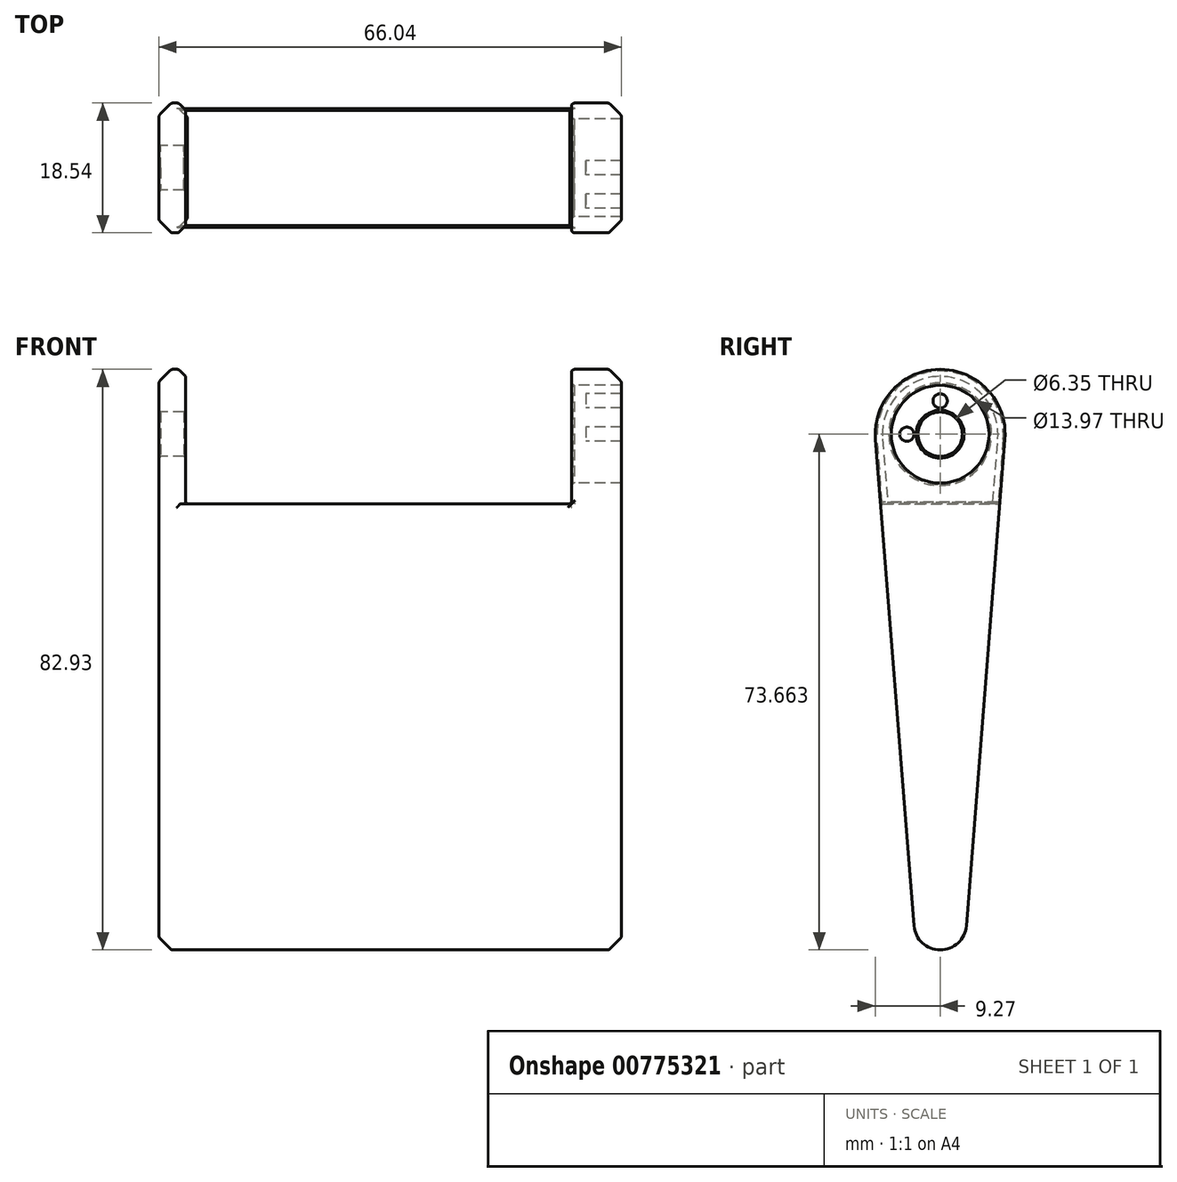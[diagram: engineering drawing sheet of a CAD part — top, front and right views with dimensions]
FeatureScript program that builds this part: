
annotation { "Feature Type Name" : "Feature", "Feature Type Description" : "" }
export const myFeature = defineFeature(function(context is Context, id is Id, definition is map)
    precondition{}
    {
        {
            var Q0;
            Q0=qCreatedBy(makeId("Right.planeOp"),FACE);
            var sketch = newSketch(context, id + "F0", { "sketchPlane" : qUnion([Q0])});
            skCircle(sketch, "E0", {"center": v(0, 54.12) * mm, "radius": 9.27 * mm});
            skCircle(sketch, "E1", {"center": v(0, -15.79) * mm, "radius": 3.75 * mm});
            skCircle(sketch, "E2", {"center": v(0, 54.12) * mm, "radius": 6.99 * mm});
            skCircle(sketch, "E3", {"center": v(0, 54.12) * mm, "radius": 3.18 * mm});
            skLineSegment(sketch, "E4", {"start": v(-9.24, 53.4) * mm, "end": v(-3.74, -16.08) * mm});
            skLineSegment(sketch, "E5", {"start": v(9.24, 53.4) * mm, "end": v(3.74, -16.08) * mm});
            skSolve(sketch);
        }
        {
            var Q0;
            {var subQ0=sQuery(id+"F0.wireOp",EDGE,"E4");Q0=makeQuery(id+"F0.imprint","IMPRINT",FACE,{"disambiguationData":[TD([[makeQuery(id+"F0.imprint","IMPRINT",EDGE,{"derivedFrom":subQ0}),1.0]])]});}
            var Q1;
            Q1=makeQuery(id+"F0.imprint","IMPRINT",FACE,{"disambiguationData":[TD([[makeQuery(id+"F0.imprint","IMPRINT",EDGE,{"derivedFrom":sQuery(id+"F0.wireOp",EDGE,"E2")}),-1.0]])]});
            var Q2;
            Q2=makeQuery(id+"F0.imprint","IMPRINT",FACE,{"disambiguationData":[TD([[makeQuery(id+"F0.imprint","IMPRINT",EDGE,{"derivedFrom":sQuery(id+"F0.wireOp",EDGE,"E2")}),1.0]])]});
            var Q3;
            {var subQ0=sQuery(id+"F0.wireOp",EDGE,"E1");var subQ1=makeQuery(id+"F0.imprint","INTERSECT",VERTEX,{"derivedFrom":[subQ0,sQuery(id+"F0.wireOp",EDGE,"E4")]});Q3=makeQuery(id+"F0.imprint","IMPRINT",FACE,{"disambiguationData":[TD([[makeQuery(id+"F0.imprint","IMPRINT",EDGE,{"disambiguationData":[TD([[subQ1,-1.0]])],"derivedFrom":subQ0}),1.0]])]});}
            extrude(context, id + "F1", {"entities" : qUnion([Q0, Q1, Q2, Q3]), "depth" : 66.04 * mm, "offsetDistance" : 25.4 * mm});
        }
        {
            var Q0;
            Q0=makeQuery(id+"F0.imprint","IMPRINT",FACE,{"disambiguationData":[TD([[makeQuery(id+"F0.imprint","IMPRINT",EDGE,{"derivedFrom":sQuery(id+"F0.wireOp",EDGE,"E2")}),-1.0]])]});
            var Q1;
            Q1=makeQuery(id+"F0.imprint","IMPRINT",FACE,{"disambiguationData":[TD([[makeQuery(id+"F0.imprint","IMPRINT",EDGE,{"derivedFrom":sQuery(id+"F0.wireOp",EDGE,"E2")}),1.0]])]});
            extrude(context, id + "F2", {"entities" : qUnion([Q0, Q1]), "operationType" : NewBodyOperationType.REMOVE, "depth" : 56.4 * mm, "offsetDistance" : 25.4 * mm});
        }
        {
            var Q0;
            Q0=makeQuery(id+"F0.imprint","IMPRINT",FACE,{"disambiguationData":[TD([[makeQuery(id+"F0.imprint","IMPRINT",EDGE,{"derivedFrom":sQuery(id+"F0.wireOp",EDGE,"E2")}),1.0]])]});
            extrude(context, id + "F3", {"entities" : qUnion([Q0]), "operationType" : NewBodyOperationType.REMOVE, "depth" : 60.96 * mm, "offsetDistance" : 25.4 * mm});
        }
        {
            var Q0;
            Q0=makeQuery(id+"F3.boolean.opBoolean","COPY",FACE,{"derivedFrom":makeQuery(id+"F3.opExtrude","CAP_FACE",FACE,{"disambiguationData":[OSD([sQuery(id+"F0.wireOp",EDGE,"E2"),sQuery(id+"F0.wireOp",EDGE,"E3")])],"isStart":false})});
            var sketch = newSketch(context, id + "F4", { "sketchPlane" : qUnion([Q0])});
            skCircle(sketch, "E6", {"center": v(0, 54.12) * mm, "radius": 4.76 * mm});
            skCircle(sketch, "E7", {"center": v(4.76, 54.12) * mm, "radius": 1.02 * mm});
            skCircle(sketch, "E8.1.0", {"center": v(3.37, 57.49) * mm, "radius": 1.02 * mm});
            skCircle(sketch, "E8.2.0", {"center": v(0, 58.88) * mm, "radius": 1.02 * mm});
            skCircle(sketch, "E8.3.0", {"center": v(-3.37, 57.49) * mm, "radius": 1.02 * mm});
            skCircle(sketch, "E8.4.0", {"center": v(-4.76, 54.12) * mm, "radius": 1.02 * mm});
            skCircle(sketch, "E8.5.0", {"center": v(-3.37, 50.76) * mm, "radius": 1.02 * mm});
            skCircle(sketch, "E8.6.0", {"center": v(0, 49.36) * mm, "radius": 1.02 * mm});
            skCircle(sketch, "E8.7.0", {"center": v(3.37, 50.76) * mm, "radius": 1.02 * mm});
            skLineSegment(sketch, "E8.anchor1", {"start": v(0, 54.12) * mm, "end": v(4.76, 54.12) * mm, "construction": true});
            skLineSegment(sketch, "E8.anchor2", {"start": v(0, 54.12) * mm, "end": v(3.37, 50.76) * mm, "construction": true});
            skSolve(sketch);
        }
        {
            var Q0;
            {var subQ0=sQuery(id+"F4.wireOp",EDGE,"E7");var subQ1=sQuery(id+"F4.wireOp",EDGE,"E6");var subQ2=makeQuery(id+"F4.imprint","INTERSECT",VERTEX,{"disambiguationData":[OD(0.0)],"derivedFrom":[subQ1,subQ0]});Q0=makeQuery(id+"F4.imprint","IMPRINT",FACE,{"disambiguationData":[TD([[makeQuery(id+"F4.imprint","IMPRINT",EDGE,{"disambiguationData":[TD([[subQ2,1.0]])],"derivedFrom":subQ1}),-1.0]])]});}
            var Q1;
            {var subQ0=sQuery(id+"F4.wireOp",EDGE,"E7");var subQ1=sQuery(id+"F4.wireOp",EDGE,"E6");var subQ2=makeQuery(id+"F4.imprint","INTERSECT",VERTEX,{"disambiguationData":[OD(0.0)],"derivedFrom":[subQ1,subQ0]});Q1=makeQuery(id+"F4.imprint","IMPRINT",FACE,{"disambiguationData":[TD([[makeQuery(id+"F4.imprint","IMPRINT",EDGE,{"disambiguationData":[TD([[subQ2,1.0]])],"derivedFrom":subQ1}),1.0]])]});}
            var Q2;
            {var subQ0=sQuery(id+"F4.wireOp",EDGE,"E8.1.0");var subQ1=sQuery(id+"F4.wireOp",EDGE,"E6");var subQ2=makeQuery(id+"F4.imprint","INTERSECT",VERTEX,{"disambiguationData":[OD(0.0)],"derivedFrom":[subQ1,subQ0]});Q2=makeQuery(id+"F4.imprint","IMPRINT",FACE,{"disambiguationData":[TD([[makeQuery(id+"F4.imprint","IMPRINT",EDGE,{"disambiguationData":[TD([[subQ2,-1.0]])],"derivedFrom":subQ1}),-1.0]])]});}
            var Q3;
            {var subQ0=sQuery(id+"F4.wireOp",EDGE,"E8.1.0");var subQ1=sQuery(id+"F4.wireOp",EDGE,"E6");var subQ2=makeQuery(id+"F4.imprint","INTERSECT",VERTEX,{"disambiguationData":[OD(0.0)],"derivedFrom":[subQ1,subQ0]});Q3=makeQuery(id+"F4.imprint","IMPRINT",FACE,{"disambiguationData":[TD([[makeQuery(id+"F4.imprint","IMPRINT",EDGE,{"disambiguationData":[TD([[subQ2,-1.0]])],"derivedFrom":subQ1}),1.0]])]});}
            var Q4;
            {var subQ0=sQuery(id+"F4.wireOp",EDGE,"E8.2.0");var subQ1=sQuery(id+"F4.wireOp",EDGE,"E6");var subQ2=makeQuery(id+"F4.imprint","INTERSECT",VERTEX,{"disambiguationData":[OD(0.0)],"derivedFrom":[subQ1,subQ0]});Q4=makeQuery(id+"F4.imprint","IMPRINT",FACE,{"disambiguationData":[TD([[makeQuery(id+"F4.imprint","IMPRINT",EDGE,{"disambiguationData":[TD([[subQ2,-1.0]])],"derivedFrom":subQ1}),1.0]])]});}
            var Q5;
            {var subQ0=sQuery(id+"F4.wireOp",EDGE,"E8.2.0");var subQ1=sQuery(id+"F4.wireOp",EDGE,"E6");var subQ2=makeQuery(id+"F4.imprint","INTERSECT",VERTEX,{"disambiguationData":[OD(0.0)],"derivedFrom":[subQ1,subQ0]});Q5=makeQuery(id+"F4.imprint","IMPRINT",FACE,{"disambiguationData":[TD([[makeQuery(id+"F4.imprint","IMPRINT",EDGE,{"disambiguationData":[TD([[subQ2,-1.0]])],"derivedFrom":subQ1}),-1.0]])]});}
            var Q6;
            {var subQ0=sQuery(id+"F4.wireOp",EDGE,"E8.3.0");var subQ1=sQuery(id+"F4.wireOp",EDGE,"E6");var subQ2=makeQuery(id+"F4.imprint","INTERSECT",VERTEX,{"disambiguationData":[OD(0.0)],"derivedFrom":[subQ1,subQ0]});Q6=makeQuery(id+"F4.imprint","IMPRINT",FACE,{"disambiguationData":[TD([[makeQuery(id+"F4.imprint","IMPRINT",EDGE,{"disambiguationData":[TD([[subQ2,-1.0]])],"derivedFrom":subQ1}),1.0]])]});}
            var Q7;
            {var subQ0=sQuery(id+"F4.wireOp",EDGE,"E8.3.0");var subQ1=sQuery(id+"F4.wireOp",EDGE,"E6");var subQ2=makeQuery(id+"F4.imprint","INTERSECT",VERTEX,{"disambiguationData":[OD(0.0)],"derivedFrom":[subQ1,subQ0]});Q7=makeQuery(id+"F4.imprint","IMPRINT",FACE,{"disambiguationData":[TD([[makeQuery(id+"F4.imprint","IMPRINT",EDGE,{"disambiguationData":[TD([[subQ2,-1.0]])],"derivedFrom":subQ1}),-1.0]])]});}
            var Q8;
            {var subQ0=sQuery(id+"F4.wireOp",EDGE,"E8.4.0");var subQ1=sQuery(id+"F4.wireOp",EDGE,"E6");var subQ2=makeQuery(id+"F4.imprint","INTERSECT",VERTEX,{"disambiguationData":[OD(0.0)],"derivedFrom":[subQ1,subQ0]});Q8=makeQuery(id+"F4.imprint","IMPRINT",FACE,{"disambiguationData":[TD([[makeQuery(id+"F4.imprint","IMPRINT",EDGE,{"disambiguationData":[TD([[subQ2,-1.0]])],"derivedFrom":subQ1}),1.0]])]});}
            var Q9;
            {var subQ0=sQuery(id+"F4.wireOp",EDGE,"E8.4.0");var subQ1=sQuery(id+"F4.wireOp",EDGE,"E6");var subQ2=makeQuery(id+"F4.imprint","INTERSECT",VERTEX,{"disambiguationData":[OD(0.0)],"derivedFrom":[subQ1,subQ0]});Q9=makeQuery(id+"F4.imprint","IMPRINT",FACE,{"disambiguationData":[TD([[makeQuery(id+"F4.imprint","IMPRINT",EDGE,{"disambiguationData":[TD([[subQ2,-1.0]])],"derivedFrom":subQ1}),-1.0]])]});}
            var Q10;
            {var subQ0=sQuery(id+"F4.wireOp",EDGE,"E8.5.0");var subQ1=sQuery(id+"F4.wireOp",EDGE,"E6");var subQ2=makeQuery(id+"F4.imprint","INTERSECT",VERTEX,{"disambiguationData":[OD(0.0)],"derivedFrom":[subQ1,subQ0]});Q10=makeQuery(id+"F4.imprint","IMPRINT",FACE,{"disambiguationData":[TD([[makeQuery(id+"F4.imprint","IMPRINT",EDGE,{"disambiguationData":[TD([[subQ2,-1.0]])],"derivedFrom":subQ1}),1.0]])]});}
            var Q11;
            {var subQ0=sQuery(id+"F4.wireOp",EDGE,"E8.5.0");var subQ1=sQuery(id+"F4.wireOp",EDGE,"E6");var subQ2=makeQuery(id+"F4.imprint","INTERSECT",VERTEX,{"disambiguationData":[OD(0.0)],"derivedFrom":[subQ1,subQ0]});Q11=makeQuery(id+"F4.imprint","IMPRINT",FACE,{"disambiguationData":[TD([[makeQuery(id+"F4.imprint","IMPRINT",EDGE,{"disambiguationData":[TD([[subQ2,-1.0]])],"derivedFrom":subQ1}),-1.0]])]});}
            var Q12;
            {var subQ0=sQuery(id+"F4.wireOp",EDGE,"E8.6.0");var subQ1=sQuery(id+"F4.wireOp",EDGE,"E6");var subQ2=makeQuery(id+"F4.imprint","INTERSECT",VERTEX,{"disambiguationData":[OD(0.0)],"derivedFrom":[subQ1,subQ0]});Q12=makeQuery(id+"F4.imprint","IMPRINT",FACE,{"disambiguationData":[TD([[makeQuery(id+"F4.imprint","IMPRINT",EDGE,{"disambiguationData":[TD([[subQ2,-1.0]])],"derivedFrom":subQ1}),1.0]])]});}
            var Q13;
            {var subQ0=sQuery(id+"F4.wireOp",EDGE,"E8.7.0");var subQ1=sQuery(id+"F4.wireOp",EDGE,"E6");var subQ2=makeQuery(id+"F4.imprint","INTERSECT",VERTEX,{"disambiguationData":[OD(0.0)],"derivedFrom":[subQ1,subQ0]});Q13=makeQuery(id+"F4.imprint","IMPRINT",FACE,{"disambiguationData":[TD([[makeQuery(id+"F4.imprint","IMPRINT",EDGE,{"disambiguationData":[TD([[subQ2,-1.0]])],"derivedFrom":subQ1}),1.0]])]});}
            var Q14;
            {var subQ0=sQuery(id+"F4.wireOp",EDGE,"E8.7.0");var subQ1=sQuery(id+"F4.wireOp",EDGE,"E6");var subQ2=makeQuery(id+"F4.imprint","INTERSECT",VERTEX,{"disambiguationData":[OD(0.0)],"derivedFrom":[subQ1,subQ0]});Q14=makeQuery(id+"F4.imprint","IMPRINT",FACE,{"disambiguationData":[TD([[makeQuery(id+"F4.imprint","IMPRINT",EDGE,{"disambiguationData":[TD([[subQ2,-1.0]])],"derivedFrom":subQ1}),-1.0]])]});}
            var Q15;
            {var subQ0=sQuery(id+"F4.wireOp",EDGE,"E8.6.0");var subQ1=sQuery(id+"F4.wireOp",EDGE,"E6");var subQ2=makeQuery(id+"F4.imprint","INTERSECT",VERTEX,{"disambiguationData":[OD(0.0)],"derivedFrom":[subQ1,subQ0]});Q15=makeQuery(id+"F4.imprint","IMPRINT",FACE,{"disambiguationData":[TD([[makeQuery(id+"F4.imprint","IMPRINT",EDGE,{"disambiguationData":[TD([[subQ2,-1.0]])],"derivedFrom":subQ1}),-1.0]])]});}
            extrude(context, id + "F5", {"entities" : qUnion([Q0, Q1, Q2, Q3, Q4, Q5, Q6, Q7, Q8, Q9, Q10, Q11, Q12, Q13, Q14, Q15]), "operationType" : NewBodyOperationType.REMOVE, "oppositeDirection" : true, "depth" : 25.4 * mm, "offsetDistance" : 25.4 * mm});
        }
        {
            var Q0;
            Q0=makeQuery(id+"F0.imprint","IMPRINT",FACE,{"disambiguationData":[TD([[makeQuery(id+"F0.imprint","IMPRINT",EDGE,{"derivedFrom":sQuery(id+"F0.wireOp",EDGE,"E2")}),-1.0]])]});
            extrude(context, id + "F6", {"entities" : qUnion([Q0]), "operationType" : NewBodyOperationType.ADD, "depth" : 5.08 * mm, "offsetDistance" : 25.4 * mm});
        }
        {
            var Q0;
            Q0=makeQuery(id+"F0.imprint","IMPRINT",FACE,{"disambiguationData":[TD([[makeQuery(id+"F0.imprint","IMPRINT",EDGE,{"derivedFrom":sQuery(id+"F0.wireOp",EDGE,"E2")}),1.0]])]});
            extrude(context, id + "F7", {"entities" : qUnion([Q0]), "operationType" : NewBodyOperationType.ADD, "depth" : 4.57 * mm, "offsetDistance" : 25.4 * mm});
        }
        {
            var Q0;
            Q0=qCreatedBy(makeId("Front.planeOp"),FACE);
            var sketch = newSketch(context, id + "F8", { "sketchPlane" : qUnion([Q0])});
            skLineSegment(sketch, "E9.bottom", {"start": v(58.93, 69.6) * mm, "end": v(3.8, 69.6) * mm});
            skLineSegment(sketch, "E9.top", {"start": v(58.93, 44.2) * mm, "end": v(3.81, 44.2) * mm});
            skLineSegment(sketch, "E9.left", {"start": v(58.93, 69.6) * mm, "end": v(58.93, 44.2) * mm});
            skLineSegment(sketch, "E9.right", {"start": v(3.8, 69.6) * mm, "end": v(3.81, 44.2) * mm});
            skSolve(sketch);
        }
        {
            var Q0;
            Q0=makeQuery(id+"F8.imprint","IMPRINT",FACE,{"disambiguationData":[TD([[makeQuery(id+"F8.imprint","IMPRINT",EDGE,{"derivedFrom":sQuery(id+"F8.wireOp",EDGE,"E9.bottom")}),1.0]])]});
            extrude(context, id + "F9", {"entities" : qUnion([Q0]), "operationType" : NewBodyOperationType.REMOVE, "oppositeDirection" : true, "depth" : 25.4 * mm, "offsetDistance" : 25.4 * mm});
        }
        {
            var Q0;
            Q0=makeQuery(id+"F8.imprint","IMPRINT",FACE,{"disambiguationData":[TD([[makeQuery(id+"F8.imprint","IMPRINT",EDGE,{"derivedFrom":sQuery(id+"F8.wireOp",EDGE,"E9.bottom")}),1.0]])]});
            extrude(context, id + "F10", {"entities" : qUnion([Q0]), "operationType" : NewBodyOperationType.REMOVE, "depth" : 25.4 * mm, "offsetDistance" : 25.4 * mm});
        }
        {
            var Q0;
            Q0=makeQuery(id+"F10.boolean.opBoolean","INTERSECT",EDGE,{"derivedFrom":[makeQuery(id+"F3.boolean.opBoolean","COPY",FACE,{"derivedFrom":makeQuery(id+"F3.opExtrude","SWEPT_FACE",FACE,{"disambiguationData":[OSD([sQuery(id+"F0.wireOp",EDGE,"E2")])]})}),makeQuery(id+"F10.opExtrude","SWEPT_FACE",FACE,{"disambiguationData":[OSD([sQuery(id+"F8.wireOp",EDGE,"E9.left")])]})]});
            chamfer(context, id + "F11", {"entities" : qUnion([Q0]), "width" : 0.25 * mm, "tangentPropagation" : true});
        }
        {
            var Q0;
            {var subQ0=sQuery(id+"F8.wireOp",EDGE,"E9.left");Q0=makeQuery(id+"F10.boolean.opBoolean","MERGE",FACE,{"derivedFrom":[makeQuery(id+"F9.boolean.opBoolean","COPY",FACE,{"derivedFrom":makeQuery(id+"F9.opExtrude","SWEPT_FACE",FACE,{"disambiguationData":[OSD([subQ0])]})}),makeQuery(id+"F10.opExtrude","SWEPT_FACE",FACE,{"disambiguationData":[OSD([subQ0])]})]});}
            chamfer(context, id + "F12", {"entities" : qUnion([Q0]), "width" : 0.25 * mm, "tangentPropagation" : true});
        }
        {
            var Q0;
            Q0=makeQuery(id+"F10.boolean.opBoolean","INTERSECT",EDGE,{"derivedFrom":[makeQuery(id+"F1.opExtrude","SWEPT_FACE",FACE,{"disambiguationData":[OSD([sQuery(id+"F0.wireOp",EDGE,"E4")])]}),makeQuery(id+"F10.opExtrude","SWEPT_FACE",FACE,{"disambiguationData":[OSD([sQuery(id+"F8.wireOp",EDGE,"E9.right")])]})]});
            var Q1;
            Q1=makeQuery(id+"F10.boolean.opBoolean","INTERSECT",EDGE,{"derivedFrom":[makeQuery(id+"F6.opExtrude","SWEPT_FACE",FACE,{"disambiguationData":[OSD([sQuery(id+"F0.wireOp",EDGE,"E0")])]}),makeQuery(id+"F10.opExtrude","SWEPT_FACE",FACE,{"disambiguationData":[OSD([sQuery(id+"F8.wireOp",EDGE,"E9.right")])]})]});
            var Q2;
            Q2=makeQuery(id+"F9.boolean.opBoolean","INTERSECT",EDGE,{"derivedFrom":[makeQuery(id+"F1.opExtrude","SWEPT_FACE",FACE,{"disambiguationData":[OSD([sQuery(id+"F0.wireOp",EDGE,"E5")])]}),makeQuery(id+"F9.opExtrude","SWEPT_FACE",FACE,{"disambiguationData":[OSD([sQuery(id+"F8.wireOp",EDGE,"E9.right")])]})]});
            chamfer(context, id + "F13", {"entities" : qUnion([Q0, Q1, Q2]), "width" : 1.02 * mm, "tangentPropagation" : true});
        }
        {
            var Q0;
            Q0=makeQuery(id+"F1.opExtrude","CAP_EDGE",EDGE,{"disambiguationData":[OSD([sQuery(id+"F0.wireOp",EDGE,"E4")])],"isStart":false});
            var Q1;
            Q1=makeQuery(id+"F1.opExtrude","CAP_EDGE",EDGE,{"disambiguationData":[OSD([sQuery(id+"F0.wireOp",EDGE,"E0")])],"isStart":false});
            var Q2;
            Q2=makeQuery(id+"F1.opExtrude","CAP_EDGE",EDGE,{"disambiguationData":[OSD([sQuery(id+"F0.wireOp",EDGE,"E5")])],"isStart":false});
            var Q3;
            Q3=makeQuery(id+"F1.opExtrude","CAP_EDGE",EDGE,{"disambiguationData":[OSD([sQuery(id+"F0.wireOp",EDGE,"E1")])],"isStart":false});
            chamfer(context, id + "F14", {"entities" : qUnion([Q0, Q1, Q2, Q3]), "width" : 1.78 * mm, "tangentPropagation" : true});
        }
        {
            var Q0;
            Q0=makeQuery(id+"F1.opExtrude","CAP_EDGE",EDGE,{"disambiguationData":[OSD([sQuery(id+"F0.wireOp",EDGE,"E5")])],"isStart":true});
            var Q1;
            Q1=makeQuery(id+"F1.opExtrude","CAP_EDGE",EDGE,{"disambiguationData":[OSD([sQuery(id+"F0.wireOp",EDGE,"E4")])],"isStart":true});
            var Q2;
            Q2=makeQuery(id+"F6.opExtrude","CAP_EDGE",EDGE,{"disambiguationData":[OSD([sQuery(id+"F0.wireOp",EDGE,"E0")])],"isStart":true});
            var Q3;
            Q3=makeQuery(id+"F1.opExtrude","CAP_EDGE",EDGE,{"disambiguationData":[OSD([sQuery(id+"F0.wireOp",EDGE,"E1")])],"isStart":true});
            chamfer(context, id + "F15", {"entities" : qUnion([Q0, Q1, Q2, Q3]), "width" : 1.78 * mm, "tangentPropagation" : true});
        }
        {
            var Q0;
            Q0=makeQuery(id+"F1.opExtrude","CAP_EDGE",EDGE,{"disambiguationData":[OSD([sQuery(id+"F0.wireOp",EDGE,"E3")])],"isStart":false});
            var Q1;
            Q1=makeQuery(id+"F10.boolean.opBoolean","INTERSECT",EDGE,{"derivedFrom":[makeQuery(id+"F7.opExtrude","SWEPT_FACE",FACE,{"disambiguationData":[OSD([sQuery(id+"F0.wireOp",EDGE,"E3")])]}),makeQuery(id+"F10.opExtrude","SWEPT_FACE",FACE,{"disambiguationData":[OSD([sQuery(id+"F8.wireOp",EDGE,"E9.right")])]})]});
            var Q2;
            Q2=makeQuery(id+"F3.boolean.opBoolean","COPY",EDGE,{"derivedFrom":makeQuery(id+"F3.opExtrude","CAP_EDGE",EDGE,{"disambiguationData":[OSD([sQuery(id+"F0.wireOp",EDGE,"E2")])],"isStart":false})});
            var Q3;
            {var subQ0=makeQuery(id+"F3.boolean.opBoolean","COPY",FACE,{"derivedFrom":makeQuery(id+"F3.opExtrude","SWEPT_FACE",FACE,{"disambiguationData":[OSD([sQuery(id+"F0.wireOp",EDGE,"E2")])]})});Q3=makeQuery(id+"F11.opChamfer","BLEND_EDGE",EDGE,{"blendedFrom":[makeQuery(id+"F10.boolean.opBoolean","INTERSECT",EDGE,{"derivedFrom":[subQ0,makeQuery(id+"F10.opExtrude","SWEPT_FACE",FACE,{"disambiguationData":[OSD([sQuery(id+"F8.wireOp",EDGE,"E9.left")])]})]}),subQ0],"blendedInto":[subQ0]});}
            var Q4;
            Q4=makeQuery(id+"F3.boolean.opBoolean","COPY",EDGE,{"derivedFrom":makeQuery(id+"F3.opExtrude","CAP_EDGE",EDGE,{"disambiguationData":[OSD([sQuery(id+"F0.wireOp",EDGE,"E3")])],"isStart":false})});
            var Q5;
            Q5=makeQuery(id+"F7.opExtrude","CAP_EDGE",EDGE,{"disambiguationData":[OSD([sQuery(id+"F0.wireOp",EDGE,"E3")])],"isStart":true});
            chamfer(context, id + "F16", {"entities" : qUnion([Q0, Q1, Q2, Q3, Q4, Q5]), "width" : 0.25 * mm, "tangentPropagation" : true});
        }
        {
            var Q0;
            {var subQ0=sQuery(id+"F8.wireOp",EDGE,"E9.right");var subQ1=sQuery(id+"F8.wireOp",EDGE,"E9.top");Q0=makeQuery(id+"F10.boolean.opBoolean","MERGE",EDGE,{"derivedFrom":[makeQuery(id+"F9.boolean.opBoolean","COPY",EDGE,{"derivedFrom":makeQuery(id+"F9.opExtrude","SWEPT_EDGE",EDGE,{"disambiguationData":[OSD([subQ1,subQ0])]})}),makeQuery(id+"F10.opExtrude","SWEPT_EDGE",EDGE,{"disambiguationData":[OSD([subQ1,subQ0])]})]});}
            chamfer(context, id + "F17", {"entities" : qUnion([Q0]), "width" : 0.25 * mm, "tangentPropagation" : true});
        }
        {
            var Q0;
            Q0=makeQuery(id+"F1.opExtrude","SWEPT_FACE",FACE,{"disambiguationData":[OSD([sQuery(id+"F0.wireOp",EDGE,"E5")])]});
            var Q1;
            {var subQ0=sQuery(id+"F0.wireOp",EDGE,"E0");Q1=makeQuery(id+"F14.opChamfer","BLEND_EDGE",EDGE,{"blendedFrom":[makeQuery(id+"F1.opExtrude","CAP_EDGE",EDGE,{"disambiguationData":[OSD([subQ0])],"isStart":false}),makeQuery(id+"F1.opExtrude","SWEPT_FACE",FACE,{"disambiguationData":[OSD([subQ0])]})],"blendedInto":[makeQuery(id+"F1.opExtrude","SWEPT_FACE",FACE,{"disambiguationData":[OSD([subQ0])]})]});}
            var Q2;
            {var subQ0=sQuery(id+"F0.wireOp",EDGE,"E4");Q2=makeQuery(id+"F14.opChamfer","BLEND_EDGE",EDGE,{"blendedFrom":[makeQuery(id+"F1.opExtrude","CAP_EDGE",EDGE,{"disambiguationData":[OSD([subQ0])],"isStart":false}),makeQuery(id+"F1.opExtrude","SWEPT_FACE",FACE,{"disambiguationData":[OSD([subQ0])]})],"blendedInto":[makeQuery(id+"F1.opExtrude","SWEPT_FACE",FACE,{"disambiguationData":[OSD([subQ0])]})]});}
            var Q3;
            {var subQ0=sQuery(id+"F0.wireOp",EDGE,"E4");Q3=makeQuery(id+"F14.opChamfer","BLEND_EDGE",EDGE,{"blendedFrom":[makeQuery(id+"F1.opExtrude","CAP_EDGE",EDGE,{"disambiguationData":[OSD([subQ0])],"isStart":false}),makeQuery(id+"F1.opExtrude","CAP_FACE",FACE,{"disambiguationData":[OSD([sQuery(id+"F0.wireOp",EDGE,"E0"),sQuery(id+"F0.wireOp",EDGE,"E1"),sQuery(id+"F0.wireOp",EDGE,"E3"),subQ0,sQuery(id+"F0.wireOp",EDGE,"E5")])],"isStart":false})],"blendedInto":[makeQuery(id+"F1.opExtrude","CAP_FACE",FACE,{"disambiguationData":[OSD([sQuery(id+"F0.wireOp",EDGE,"E0"),sQuery(id+"F0.wireOp",EDGE,"E1"),sQuery(id+"F0.wireOp",EDGE,"E3"),subQ0,sQuery(id+"F0.wireOp",EDGE,"E5")])],"isStart":false})]});}
            var Q4;
            {var subQ0=makeQuery(id+"F1.opExtrude","SWEPT_FACE",FACE,{"disambiguationData":[OSD([sQuery(id+"F0.wireOp",EDGE,"E4")])]});Q4=makeQuery(id+"F12.opChamfer","BLEND_EDGE",EDGE,{"blendedFrom":[makeQuery(id+"F10.boolean.opBoolean","INTERSECT",EDGE,{"derivedFrom":[subQ0,makeQuery(id+"F10.opExtrude","SWEPT_FACE",FACE,{"disambiguationData":[OSD([sQuery(id+"F8.wireOp",EDGE,"E9.top")])]})]}),subQ0],"blendedInto":[subQ0]});}
            var Q5;
            {var subQ0=makeQuery(id+"F1.opExtrude","SWEPT_FACE",FACE,{"disambiguationData":[OSD([sQuery(id+"F0.wireOp",EDGE,"E4")])]});Q5=makeQuery(id+"F12.opChamfer","BLEND_EDGE",EDGE,{"blendedFrom":[makeQuery(id+"F10.boolean.opBoolean","INTERSECT",EDGE,{"derivedFrom":[subQ0,makeQuery(id+"F10.opExtrude","SWEPT_FACE",FACE,{"disambiguationData":[OSD([sQuery(id+"F8.wireOp",EDGE,"E9.left")])]})]}),subQ0],"blendedInto":[subQ0]});}
            var Q6;
            {var subQ0=sQuery(id+"F0.wireOp",EDGE,"E3");var subQ1=sQuery(id+"F0.wireOp",EDGE,"E2");var subQ2=sQuery(id+"F0.wireOp",EDGE,"E0");Q6=makeQuery(id+"F7.boolean.opBoolean","MERGE",FACE,{"derivedFrom":[makeQuery(id+"F6.boolean.opBoolean","MERGE",FACE,{"derivedFrom":[makeQuery(id+"F1.opExtrude","CAP_FACE",FACE,{"disambiguationData":[OSD([subQ2,sQuery(id+"F0.wireOp",EDGE,"E1"),subQ0,sQuery(id+"F0.wireOp",EDGE,"E4"),sQuery(id+"F0.wireOp",EDGE,"E5")])],"isStart":true}),makeQuery(id+"F6.opExtrude","CAP_FACE",FACE,{"disambiguationData":[OSD([subQ2,subQ1])],"isStart":true})]}),makeQuery(id+"F7.opExtrude","CAP_FACE",FACE,{"disambiguationData":[OSD([subQ1,subQ0])],"isStart":true})]});}
            var Q7;
            {var subQ0=sQuery(id+"F0.wireOp",EDGE,"E4");Q7=makeQuery(id+"F15.opChamfer","BLEND_EDGE",EDGE,{"blendedFrom":[makeQuery(id+"F1.opExtrude","CAP_EDGE",EDGE,{"disambiguationData":[OSD([subQ0])],"isStart":true}),makeQuery(id+"F1.opExtrude","SWEPT_FACE",FACE,{"disambiguationData":[OSD([subQ0])]})],"blendedInto":[makeQuery(id+"F1.opExtrude","SWEPT_FACE",FACE,{"disambiguationData":[OSD([subQ0])]})]});}
            fillet(context, id + "F18", {"entities" : qUnion([Q0, Q1, Q2, Q3, Q4, Q5, Q6, Q7]), "radius" : 0.64 * mm, "tangentPropagation" : true, "allowEdgeOverflow" : false});
        }
    });
